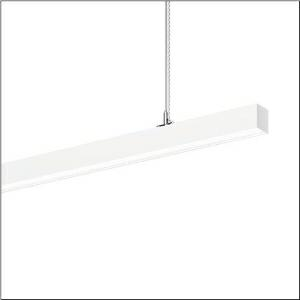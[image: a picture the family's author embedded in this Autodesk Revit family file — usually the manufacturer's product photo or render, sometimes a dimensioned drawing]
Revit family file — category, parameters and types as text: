
# Revit family: silica_r__21_51mx33db39wb_e509
name_source: partatom
category: Lighting Fixtures
units: mm (PartAtom-declared; Revit-internal decimal feet)

## family parameters
Cut with Voids When Loaded = No
Host = Face
Light Source = No
Part Type = Normal
Room Calculation Point = No
Round Connector Dimension = Use Diameter
Shared = No

## types (1)
- --- (1 x LED, 7390 lm, 51.6 W, 3000K)
    Apparent Load = 52 VA
    CIE Flux Codes = 78 96 99 55 100
    Color Rendering = 80
    Color Temperature = 3000K
    Default Elevation = 1800 mm
    Description = Silica® 21, office luminaire, primary optical cover: prismatic diffuser, of PMMA, CAT 2 (L<= 3000cd/m²), light emission: direct/indirect distribution, primary light characteristic: symmetric, installation type: suspended mounting, LED, rated luminous flux: 7.390lm, luminous efficacy: 143lm/W, light colour: 830, colour temperature: 3000K, control gear: DALI 2, with terminal, 3+2-pole, max. 2.5mm², mains connection: 220..240V, AC, 50/60Hz, rated input power: 51.6W, luminaire housing, of aluminium, traffic white (RAL 9016), length: 1.504mm, width: 53mm, height: 53mm, protection rating (complete): IP20, insulation class (complete): insulation class I (protective earthing), certification: CE, permissible operating ambient temperature: 0..+35°C, standard: EN 50419, packaging unit: 1 piece
    Height = 53 mm
    Lamp = 1 x LED
    Lamp Light Flux = 7390 lm
    Lamp Power = 51.6 W
    Lamp count = 1
    Length = 1504 mm
    Luminous efficacy = 143 lm/W
    Manufacturer = Siteco
    ModVariant = No
    Model = 51MX33DB39WB
    Mounting Place = Ceiling
    Mounting Type = Pendant
    Number of Poles = 1
    OnlyDefault = Yes
    Power Factor = 1
    Product Name = Silica® 21
    Product group = office luminaire | ceiling pendant
    ProductGroupID = 904
    Protection Class = Protection class I
    Protection Degree = IP 20
    RLX_Detail_Level = 1
    RLX_Emergency_Light_Flux = 0 lm
    RLX_Emergency_Type = 0
    RLX_Emergency_Type_DB = No
    RlxData = <blob elided: 21429 chars, md5=2415e02a>
    Socket = socket
    Standby Power = 0 W
    System Light Flux = 7390 lm
    System Power = 52 W
    Type Comments = factory setting: luminous flux: 100 % | dim-lin: 254 | 345 mA
    Type Image = l_1349007.jpg
    URL = http://relux.com
    VarID = @adj_118252
    Voltage = 0 V
    Weight = 0.00 kg
    Width = 53 mm

## geometry (parser evidence)
native form markers: Blend x4, Sweep x15
no freeform markers — native parametric forms only
